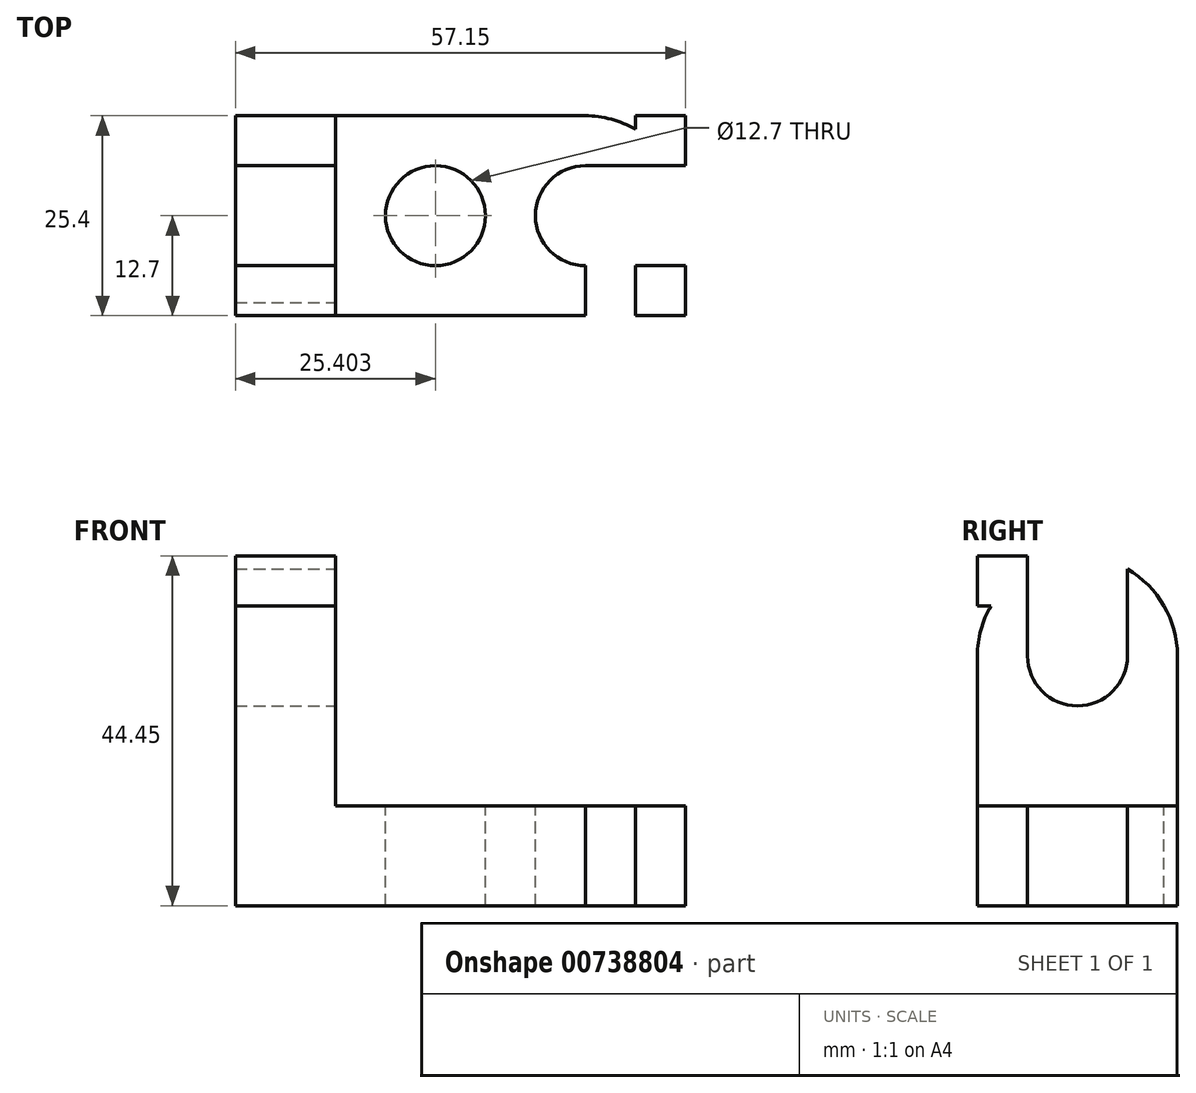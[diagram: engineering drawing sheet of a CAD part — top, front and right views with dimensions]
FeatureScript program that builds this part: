
annotation { "Feature Type Name" : "Feature", "Feature Type Description" : "" }
export const myFeature = defineFeature(function(context is Context, id is Id, definition is map)
    precondition{}
    {
        {
            var Q0;
            Q0=qCreatedBy(makeId("Front.planeOp"),FACE);
            var sketch = newSketch(context, id + "F0", { "sketchPlane" : qUnion([Q0])});
            skLineSegment(sketch, "E0.bottom", {"start": v(-34.78, 37.11) * mm, "end": v(22.37, 37.11) * mm});
            skLineSegment(sketch, "E0.top", {"start": v(-34.78, -7.34) * mm, "end": v(22.37, -7.34) * mm});
            skLineSegment(sketch, "E0.left", {"start": v(-34.78, 37.11) * mm, "end": v(-34.78, -7.34) * mm});
            skLineSegment(sketch, "E0.right", {"start": v(22.37, 37.11) * mm, "end": v(22.37, -7.34) * mm});
            skSolve(sketch);
        }
        {
            var Q0;
            Q0 = qSketchRegion(id + "F0", true);
            extrude(context, id + "F1", {"entities" : qUnion([Q0]), "depth" : 25.4 * mm, "offsetDistance" : 25.4 * mm});
        }
        {
            var Q0;
            Q0=makeQuery(id+"F1.opExtrude","CAP_FACE",FACE,{"disambiguationData":[OSD([sQuery(id+"F0.wireOp",EDGE,"E0.bottom"),sQuery(id+"F0.wireOp",EDGE,"E0.top"),sQuery(id+"F0.wireOp",EDGE,"E0.left"),sQuery(id+"F0.wireOp",EDGE,"E0.right")])],"isStart":false});
            var sketch = newSketch(context, id + "F2", { "sketchPlane" : qUnion([Q0])});
            skLineSegment(sketch, "E1", {"start": v(-22.08, 37.11) * mm, "end": v(-22.08, 5.36) * mm});
            skLineSegment(sketch, "E2", {"start": v(-22.08, 5.36) * mm, "end": v(22.37, 5.36) * mm});
            skSolve(sketch);
        }
        {
            var Q0;
            Q0 = qSketchRegion(id + "F2", true);
            var Q1;
            {var subQ0=sQuery(id+"F2.wireOp",EDGE,"E1");Q1=makeQuery(id+"F2.imprint","IMPRINT",FACE,{"disambiguationData":[TD([[makeQuery(id+"F2.imprint","IMPRINT",EDGE,{"derivedFrom":subQ0}),1.0]])]});}
            extrude(context, id + "F3", {"entities" : qUnion([Q0, Q1]), "operationType" : NewBodyOperationType.REMOVE, "endBound" : BoundingType.THROUGH_ALL, "oppositeDirection" : true, "depth" : 25.4 * mm, "offsetDistance" : 25.4 * mm});
        }
        {
            var Q0;
            Q0=makeQuery(id+"F3.boolean.opBoolean","COPY",FACE,{"derivedFrom":makeQuery(id+"F3.opExtrude","SWEPT_FACE",FACE,{"disambiguationData":[OSD([sQuery(id+"F2.wireOp",EDGE,"E2")])]})});
            var sketch = newSketch(context, id + "F4", { "sketchPlane" : qUnion([Q0])});
            skLineSegment(sketch, "E3", {"start": v(-15.73, 0) * mm, "end": v(-15.73, -25.4) * mm});
            skLineSegment(sketch, "E4", {"start": v(16.02, 0) * mm, "end": v(16.02, -25.4) * mm});
            skLineSegment(sketch, "E5", {"start": v(-3.03, 0) * mm, "end": v(-3.03, -25.4) * mm});
            skLineSegment(sketch, "E6", {"start": v(3.32, 0) * mm, "end": v(3.32, -25.4) * mm});
            skLineSegment(sketch, "E7", {"start": v(-22.08, -6.35) * mm, "end": v(22.37, -6.35) * mm});
            skLineSegment(sketch, "E8", {"start": v(-22.08, -19.05) * mm, "end": v(22.37, -19.05) * mm});
            skCircle(sketch, "E9", {"center": v(-9.38, -12.7) * mm, "radius": 6.35 * mm});
            skCircle(sketch, "E10", {"center": v(9.67, -12.7) * mm, "radius": 6.35 * mm});
            skLineSegment(sketch, "E11", {"start": v(9.67, -12.7) * mm, "end": v(9.67, 0) * mm});
            skLineSegment(sketch, "E12", {"start": v(9.67, -12.7) * mm, "end": v(9.67, -25.4) * mm});
            skArc(sketch, "E13", {"start": v(9.67, -25.4) * mm, "mid": v(22.37, -12.7) * mm, "end": v(9.67, 0) * mm});
            skSolve(sketch);
        }
        {
            var Q0;
            {var subQ0=sQuery(id+"F4.wireOp",EDGE,"E10");var subQ1=makeQuery(id+"F4.imprint","INTERSECT",VERTEX,{"derivedFrom":[sQuery(id+"F4.wireOp",EDGE,"E4"),subQ0]});Q0=makeQuery(id+"F4.imprint","IMPRINT",FACE,{"disambiguationData":[TD([[makeQuery(id+"F4.imprint","IMPRINT",EDGE,{"disambiguationData":[TD([[subQ1,-1.0]])],"derivedFrom":subQ0}),1.0]])]});}
            var Q1;
            {var subQ0=sQuery(id+"F4.wireOp",EDGE,"E10");var subQ1=makeQuery(id+"F4.imprint","INTERSECT",VERTEX,{"derivedFrom":[sQuery(id+"F4.wireOp",EDGE,"E6"),subQ0]});Q1=makeQuery(id+"F4.imprint","IMPRINT",FACE,{"disambiguationData":[TD([[makeQuery(id+"F4.imprint","IMPRINT",EDGE,{"disambiguationData":[TD([[subQ1,1.0]])],"derivedFrom":subQ0}),1.0]])]});}
            var Q2;
            {var subQ0=sQuery(id+"F4.wireOp",EDGE,"E9");var subQ1=makeQuery(id+"F4.imprint","INTERSECT",VERTEX,{"derivedFrom":[sQuery(id+"F4.wireOp",EDGE,"E5"),subQ0]});Q2=makeQuery(id+"F4.imprint","IMPRINT",FACE,{"disambiguationData":[TD([[makeQuery(id+"F4.imprint","IMPRINT",EDGE,{"disambiguationData":[TD([[subQ1,-1.0]])],"derivedFrom":subQ0}),1.0]])]});}
            var Q3;
            {var subQ7=sQuery(id+"F4.wireOp",EDGE,"E13");var subQ8=sQuery(id+"F4.wireOp",EDGE,"E4");var subQ9=makeQuery(id+"F4.imprint","INTERSECT",VERTEX,{"disambiguationData":[OD(0.0)],"derivedFrom":[subQ8,subQ7]});Q3=makeQuery(id+"F4.imprint","IMPRINT",FACE,{"disambiguationData":[TD([[makeQuery(id+"F4.imprint","IMPRINT",EDGE,{"disambiguationData":[TD([[subQ9,1.0]])],"derivedFrom":subQ7}),-1.0]])]});}
            var Q4;
            {var subQ0=sQuery(id+"F4.wireOp",EDGE,"E4");var subQ3=sQuery(id+"F4.wireOp",EDGE,"E13");var subQ4=makeQuery(id+"F4.imprint","INTERSECT",VERTEX,{"disambiguationData":[OD(0.0)],"derivedFrom":[subQ0,subQ3]});Q4=makeQuery(id+"F4.imprint","IMPRINT",FACE,{"disambiguationData":[TD([[makeQuery(id+"F4.imprint","IMPRINT",EDGE,{"disambiguationData":[TD([[subQ4,1.0]])],"derivedFrom":subQ0}),-1.0]])]});}
            var Q5;
            {var subQ0=sQuery(id+"F4.wireOp",EDGE,"E7");var subQ3=sQuery(id+"F4.wireOp",EDGE,"E13");var subQ4=makeQuery(id+"F4.imprint","INTERSECT",VERTEX,{"derivedFrom":[subQ0,subQ3]});Q5=makeQuery(id+"F4.imprint","IMPRINT",FACE,{"disambiguationData":[TD([[makeQuery(id+"F4.imprint","IMPRINT",EDGE,{"disambiguationData":[TD([[subQ4,-1.0]])],"derivedFrom":subQ0}),-1.0]])]});}
            var Q6;
            {var subQ0=sQuery(id+"F4.wireOp",EDGE,"E8");var subQ3=sQuery(id+"F4.wireOp",EDGE,"E13");var subQ4=makeQuery(id+"F4.imprint","INTERSECT",VERTEX,{"derivedFrom":[subQ0,subQ3]});Q6=makeQuery(id+"F4.imprint","IMPRINT",FACE,{"disambiguationData":[TD([[makeQuery(id+"F4.imprint","IMPRINT",EDGE,{"disambiguationData":[TD([[subQ4,-1.0]])],"derivedFrom":subQ0}),1.0]])]});}
            var Q7;
            {var subQ0=sQuery(id+"F2.wireOp",EDGE,"E2");var subQ1=makeQuery(id+"F3.boolean.opBoolean","COPY",EDGE,{"derivedFrom":makeQuery(id+"F3.opExtrude","CAP_EDGE",EDGE,{"disambiguationData":[OSD([subQ0])],"isStart":true})});var subQ8=sQuery(id+"F4.wireOp",EDGE,"E4");var subQ10=makeQuery(id+"F4.imprint","INTERSECT",VERTEX,{"derivedFrom":[subQ1,subQ8]});Q7=makeQuery(id+"F4.imprint","IMPRINT",FACE,{"disambiguationData":[TD([[makeQuery(id+"F4.imprint","IMPRINT",EDGE,{"disambiguationData":[TD([[subQ10,1.0]])],"derivedFrom":subQ8}),1.0]])]});}
            var Q8;
            {var subQ0=sQuery(id+"F4.wireOp",EDGE,"E4");var subQ1=makeQuery(id+"F3.boolean.opBoolean","COPY",EDGE,{"derivedFrom":makeQuery(id+"F3.opExtrude","CAP_EDGE",EDGE,{"disambiguationData":[OSD([sQuery(id+"F2.wireOp",EDGE,"E2")])],"isStart":true})});var subQ2=makeQuery(id+"F4.imprint","INTERSECT",VERTEX,{"derivedFrom":[subQ1,subQ0]});Q8=makeQuery(id+"F4.imprint","IMPRINT",FACE,{"disambiguationData":[TD([[makeQuery(id+"F4.imprint","IMPRINT",EDGE,{"disambiguationData":[TD([[subQ2,1.0]])],"derivedFrom":subQ0}),-1.0]])]});}
            extrude(context, id + "F5", {"entities" : qUnion([Q0, Q1, Q2, Q3, Q4, Q5, Q6, Q7, Q8]), "operationType" : NewBodyOperationType.REMOVE, "endBound" : BoundingType.THROUGH_ALL, "oppositeDirection" : true, "depth" : 25.4 * mm, "offsetDistance" : 25.4 * mm});
        }
        {
            var Q0;
            Q0=makeQuery(id+"F3.boolean.opBoolean","COPY",FACE,{"derivedFrom":makeQuery(id+"F3.opExtrude","SWEPT_FACE",FACE,{"disambiguationData":[OSD([sQuery(id+"F2.wireOp",EDGE,"E1")])]})});
            var sketch = newSketch(context, id + "F6", { "sketchPlane" : qUnion([Q0])});
            skLineSegment(sketch, "E14", {"start": v(-19.05, 5.36) * mm, "end": v(-19.05, 37.11) * mm});
            skLineSegment(sketch, "E15", {"start": v(-6.35, 37.11) * mm, "end": v(-6.35, 5.36) * mm});
            skLineSegment(sketch, "E16", {"start": v(-25.4, 18.06) * mm, "end": v(0, 18.06) * mm});
            skCircle(sketch, "E17", {"center": v(-12.7, 24.41) * mm, "radius": 6.35 * mm});
            skLineSegment(sketch, "E18", {"start": v(-25.4, 30.76) * mm, "end": v(0, 30.76) * mm});
            skLineSegment(sketch, "E19", {"start": v(-12.7, 24.41) * mm, "end": v(0, 24.41) * mm});
            skLineSegment(sketch, "E20", {"start": v(-12.7, 24.41) * mm, "end": v(-25.4, 24.41) * mm});
            skArc(sketch, "E21", {"start": v(0, 24.41) * mm, "mid": v(-12.7, 37.11) * mm, "end": v(-25.4, 24.41) * mm});
            skSolve(sketch);
        }
        {
            var Q0;
            {var subQ0=sQuery(id+"F6.wireOp",EDGE,"E18");var subQ1=sQuery(id+"F6.wireOp",EDGE,"E14");var subQ2=makeQuery(id+"F6.imprint","INTERSECT",VERTEX,{"derivedFrom":[subQ1,subQ0]});Q0=makeQuery(id+"F6.imprint","IMPRINT",FACE,{"disambiguationData":[TD([[makeQuery(id+"F6.imprint","IMPRINT",EDGE,{"disambiguationData":[TD([[subQ2,-1.0]])],"derivedFrom":subQ0}),-1.0]])]});}
            var Q1;
            {var subQ0=sQuery(id+"F6.wireOp",EDGE,"E18");var subQ1=sQuery(id+"F6.wireOp",EDGE,"E15");var subQ2=makeQuery(id+"F6.imprint","INTERSECT",VERTEX,{"derivedFrom":[subQ1,subQ0]});Q1=makeQuery(id+"F6.imprint","IMPRINT",FACE,{"disambiguationData":[TD([[makeQuery(id+"F6.imprint","IMPRINT",EDGE,{"disambiguationData":[TD([[subQ2,1.0]])],"derivedFrom":subQ0}),-1.0]])]});}
            var Q2;
            {var subQ0=sQuery(id+"F6.wireOp",EDGE,"E17");var subQ1=makeQuery(id+"F6.imprint","INTERSECT",VERTEX,{"derivedFrom":[subQ0,sQuery(id+"F6.wireOp",EDGE,"E18")]});Q2=makeQuery(id+"F6.imprint","IMPRINT",FACE,{"disambiguationData":[TD([[makeQuery(id+"F6.imprint","IMPRINT",EDGE,{"disambiguationData":[TD([[subQ1,1.0]])],"derivedFrom":subQ0}),1.0]])]});}
            var Q3;
            {var subQ0=sQuery(id+"F6.wireOp",EDGE,"E18");var subQ1=sQuery(id+"F6.wireOp",EDGE,"E14");var subQ2=makeQuery(id+"F6.imprint","INTERSECT",VERTEX,{"derivedFrom":[subQ1,subQ0]});Q3=makeQuery(id+"F6.imprint","IMPRINT",FACE,{"disambiguationData":[TD([[makeQuery(id+"F6.imprint","IMPRINT",EDGE,{"disambiguationData":[TD([[subQ2,-1.0]])],"derivedFrom":subQ1}),-1.0]])]});}
            var Q4;
            {var subQ3=sQuery(id+"F6.wireOp",EDGE,"E18");var subQ5=sQuery(id+"F2.wireOp",EDGE,"E1");var subQ6=makeQuery(id+"F3.boolean.opBoolean","COPY",EDGE,{"derivedFrom":makeQuery(id+"F3.opExtrude","CAP_EDGE",EDGE,{"disambiguationData":[OSD([subQ5])],"isStart":true})});var subQ7=makeQuery(id+"F6.imprint","INTERSECT",VERTEX,{"derivedFrom":[subQ6,subQ3]});Q4=makeQuery(id+"F6.imprint","IMPRINT",FACE,{"disambiguationData":[TD([[makeQuery(id+"F6.imprint","IMPRINT",EDGE,{"disambiguationData":[TD([[subQ7,-1.0]])],"derivedFrom":subQ3}),1.0]])]});}
            var Q5;
            {var subQ0=sQuery(id+"F6.wireOp",EDGE,"E18");var subQ3=sQuery(id+"F6.wireOp",EDGE,"E21");var subQ4=makeQuery(id+"F6.imprint","INTERSECT",VERTEX,{"disambiguationData":[OD(1.0)],"derivedFrom":[subQ0,subQ3]});Q5=makeQuery(id+"F6.imprint","IMPRINT",FACE,{"disambiguationData":[TD([[makeQuery(id+"F6.imprint","IMPRINT",EDGE,{"disambiguationData":[TD([[subQ4,-1.0]])],"derivedFrom":subQ0}),-1.0]])]});}
            var Q6;
            {var subQ0=sQuery(id+"F6.wireOp",EDGE,"E18");var subQ1=makeQuery(id+"F3.boolean.opBoolean","COPY",EDGE,{"derivedFrom":makeQuery(id+"F3.opExtrude","CAP_EDGE",EDGE,{"disambiguationData":[OSD([sQuery(id+"F2.wireOp",EDGE,"E1")])],"isStart":true})});var subQ2=makeQuery(id+"F6.imprint","INTERSECT",VERTEX,{"derivedFrom":[subQ1,subQ0]});Q6=makeQuery(id+"F6.imprint","IMPRINT",FACE,{"disambiguationData":[TD([[makeQuery(id+"F6.imprint","IMPRINT",EDGE,{"disambiguationData":[TD([[subQ2,-1.0]])],"derivedFrom":subQ0}),-1.0]])]});}
            var Q7;
            {var subQ0=sQuery(id+"F6.wireOp",EDGE,"E14");var subQ3=sQuery(id+"F6.wireOp",EDGE,"E21");var subQ4=makeQuery(id+"F6.imprint","INTERSECT",VERTEX,{"derivedFrom":[subQ0,subQ3]});Q7=makeQuery(id+"F6.imprint","IMPRINT",FACE,{"disambiguationData":[TD([[makeQuery(id+"F6.imprint","IMPRINT",EDGE,{"disambiguationData":[TD([[subQ4,-1.0]])],"derivedFrom":subQ0}),-1.0]])]});}
            var Q8;
            {var subQ0=sQuery(id+"F6.wireOp",EDGE,"E15");var subQ3=sQuery(id+"F6.wireOp",EDGE,"E21");var subQ4=makeQuery(id+"F6.imprint","INTERSECT",VERTEX,{"derivedFrom":[subQ0,subQ3]});Q8=makeQuery(id+"F6.imprint","IMPRINT",FACE,{"disambiguationData":[TD([[makeQuery(id+"F6.imprint","IMPRINT",EDGE,{"disambiguationData":[TD([[subQ4,1.0]])],"derivedFrom":subQ0}),-1.0]])]});}
            var Q9;
            {var subQ0=sQuery(id+"F6.wireOp",EDGE,"E21");var subQ1=sQuery(id+"F6.wireOp",EDGE,"E15");var subQ2=makeQuery(id+"F6.imprint","INTERSECT",VERTEX,{"derivedFrom":[subQ1,subQ0]});Q9=makeQuery(id+"F6.imprint","IMPRINT",FACE,{"disambiguationData":[TD([[makeQuery(id+"F6.imprint","IMPRINT",EDGE,{"disambiguationData":[TD([[subQ2,1.0]])],"derivedFrom":subQ0}),-1.0]])]});}
            var Q10;
            {var subQ0=sQuery(id+"F6.wireOp",EDGE,"E17");var subQ1=makeQuery(id+"F6.imprint","INTERSECT",VERTEX,{"derivedFrom":[sQuery(id+"F6.wireOp",EDGE,"E16"),subQ0]});Q10=makeQuery(id+"F6.imprint","IMPRINT",FACE,{"disambiguationData":[TD([[makeQuery(id+"F6.imprint","IMPRINT",EDGE,{"disambiguationData":[TD([[subQ1,1.0]])],"derivedFrom":subQ0}),1.0]])]});}
            extrude(context, id + "F7", {"entities" : qUnion([Q0, Q1, Q2, Q3, Q4, Q5, Q6, Q7, Q8, Q9, Q10]), "operationType" : NewBodyOperationType.REMOVE, "oppositeDirection" : true, "depth" : 25.4 * mm, "offsetDistance" : 25.4 * mm});
        }
    });
